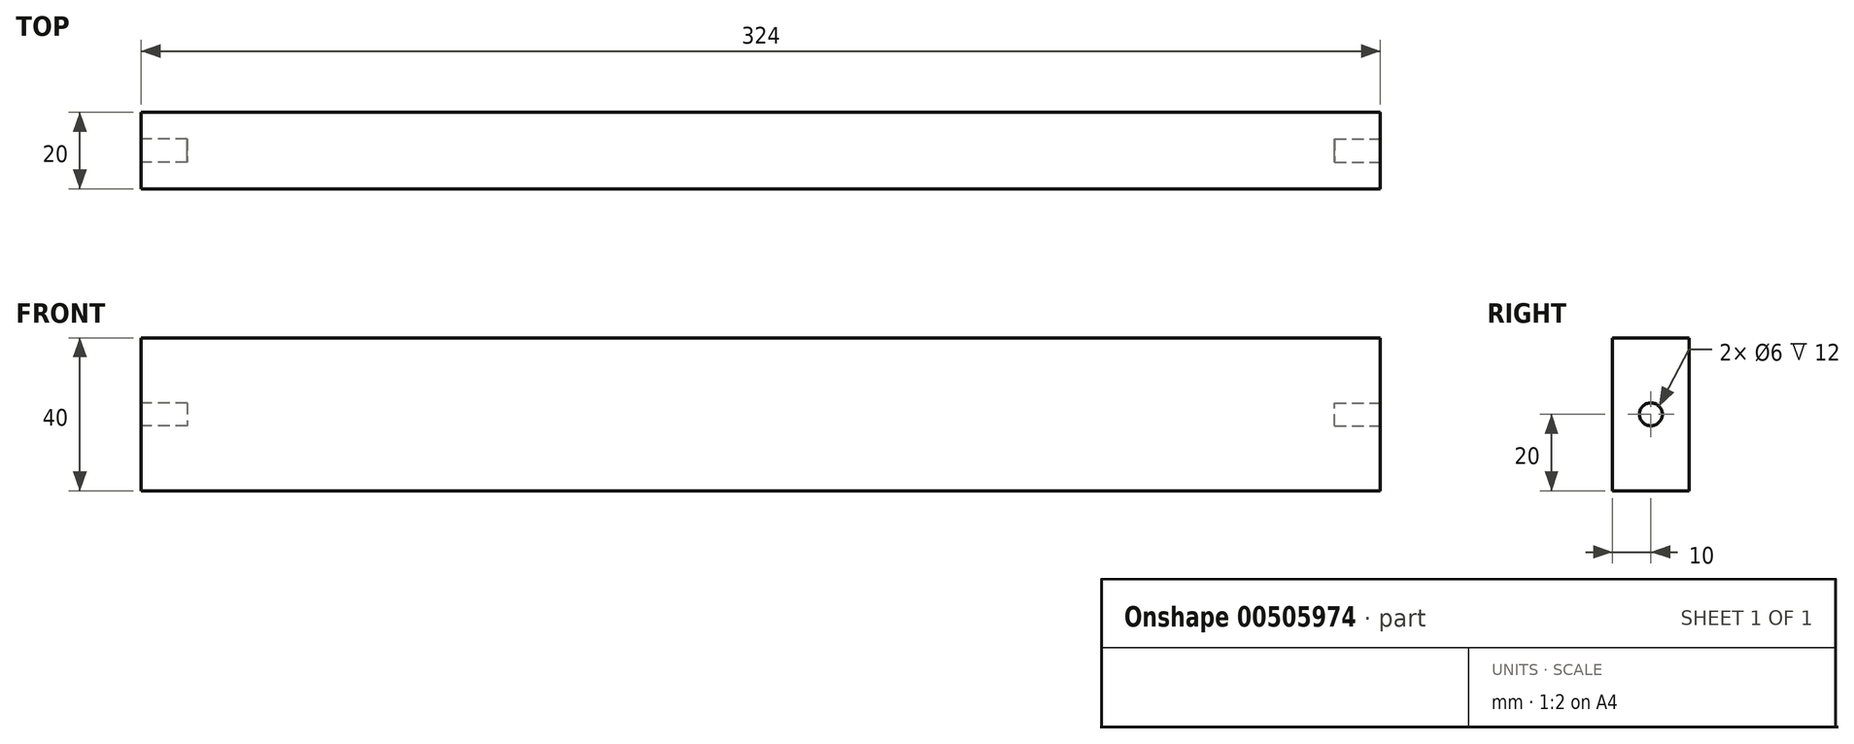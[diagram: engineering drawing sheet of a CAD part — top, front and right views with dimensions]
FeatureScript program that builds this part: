
annotation { "Feature Type Name" : "Feature", "Feature Type Description" : "" }
export const myFeature = defineFeature(function(context is Context, id is Id, definition is map)
    precondition{}
    {
        {
            var Q0;
            Q0=qCreatedBy(makeId("Front.planeOp"),FACE);
            var sketch = newSketch(context, id + "F0", { "sketchPlane" : qUnion([Q0])});
            skLineSegment(sketch, "E0.bottom", {"start": v(-154.1, 40) * mm, "end": v(169.9, 40) * mm});
            skLineSegment(sketch, "E0.top", {"start": v(-154.1, 0) * mm, "end": v(169.9, 0) * mm});
            skLineSegment(sketch, "E0.left", {"start": v(-154.1, 40) * mm, "end": v(-154.1, 0) * mm});
            skLineSegment(sketch, "E0.right", {"start": v(169.9, 40) * mm, "end": v(169.9, 0) * mm});
            skSolve(sketch);
        }
        {
            var Q0;
            Q0 = qSketchRegion(id + "F0", true);
            extrude(context, id + "F1", {"entities" : qUnion([Q0]), "depth" : 20 * mm, "offsetDistance" : 25 * mm});
        }
        {
            var Q0;
            Q0=makeQuery(id+"F1.opExtrude","SWEPT_FACE",FACE,{"disambiguationData":[OSD([sQuery(id+"F0.wireOp",EDGE,"E0.right")])]});
            var sketch = newSketch(context, id + "F2", { "sketchPlane" : qUnion([Q0])});
            skCircle(sketch, "E1", {"center": v(-10, 20) * mm, "radius": 3 * mm});
            skSolve(sketch);
        }
        {
            var Q0;
            Q0=makeQuery(id+"F1.opExtrude","SWEPT_FACE",FACE,{"disambiguationData":[OSD([sQuery(id+"F0.wireOp",EDGE,"E0.left")])]});
            var sketch = newSketch(context, id + "F3", { "sketchPlane" : qUnion([Q0])});
            skCircle(sketch, "E2", {"center": v(10, 20) * mm, "radius": 3 * mm});
            skSolve(sketch);
        }
        {
            var Q0;
            Q0 = qSketchRegion(id + "F2", true);
            extrude(context, id + "F4", {"entities" : qUnion([Q0]), "operationType" : NewBodyOperationType.REMOVE, "oppositeDirection" : true, "depth" : 12 * mm, "offsetDistance" : 25 * mm});
        }
        {
            var Q0;
            Q0=makeQuery(id+"F3.imprint","IMPRINT",FACE,{"disambiguationData":[TD([[makeQuery(id+"F3.imprint","IMPRINT",EDGE,{"derivedFrom":sQuery(id+"F3.wireOp",EDGE,"E2")}),1.0]])]});
            var Q1;
            Q1 = qSketchRegion(id + "F3", true);
            extrude(context, id + "F5", {"entities" : qUnion([Q0, Q1]), "operationType" : NewBodyOperationType.REMOVE, "oppositeDirection" : true, "depth" : 12 * mm, "offsetDistance" : 25 * mm});
        }
    });
